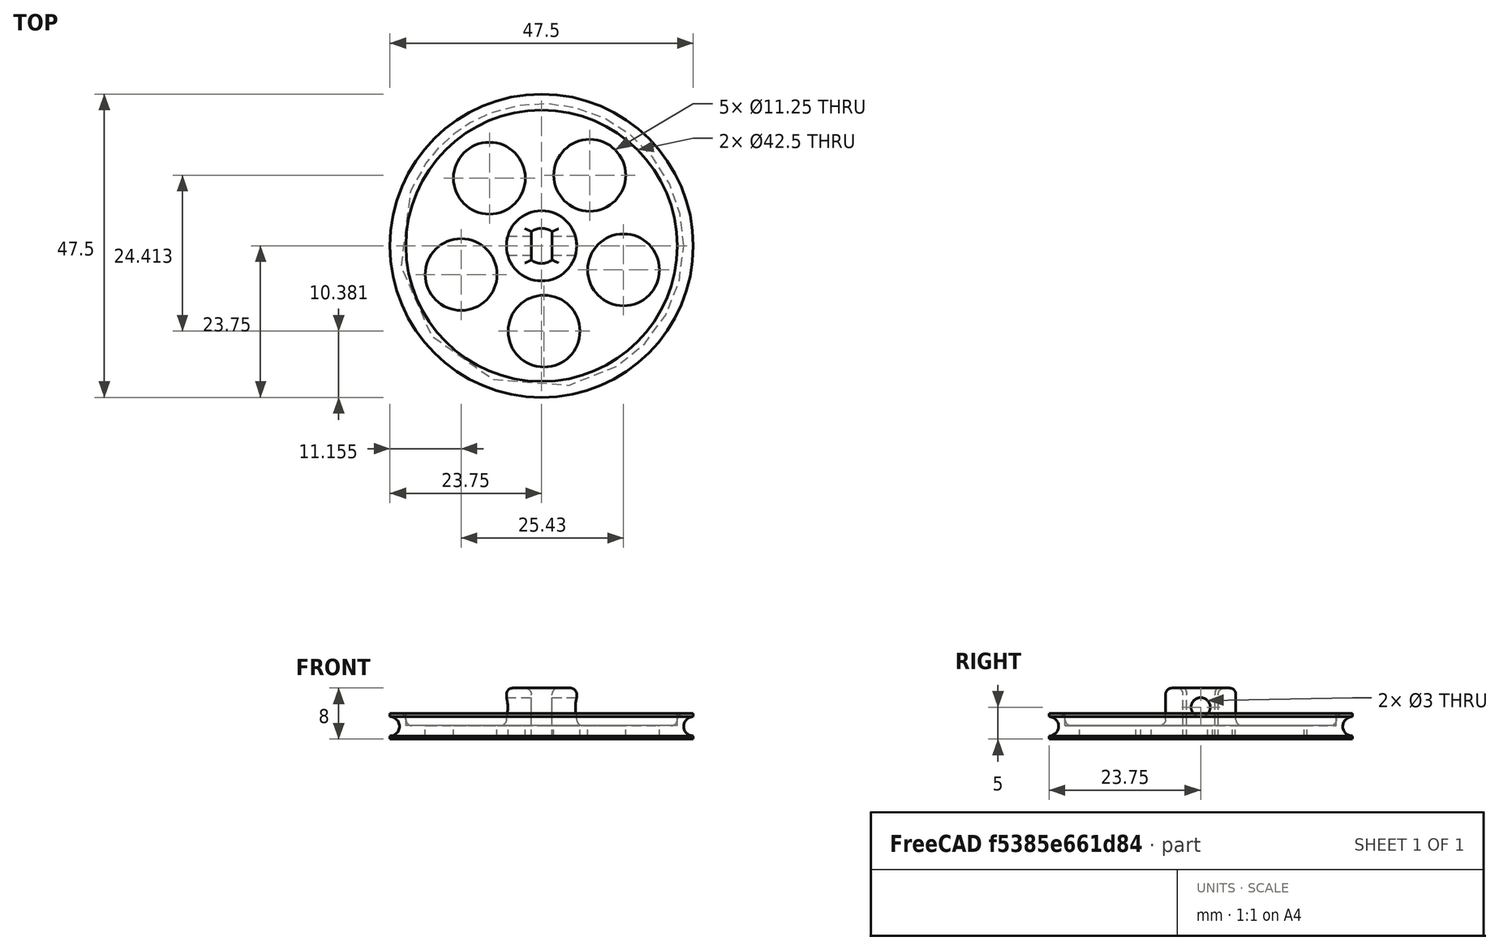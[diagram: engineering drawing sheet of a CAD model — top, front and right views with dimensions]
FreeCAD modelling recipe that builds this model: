
FCSTD DOCUMENT  (FreeCAD 0.16R6712 (Git))
Label: wheel_v02
License: All rights reserved
LicenseURL: http://en.wikipedia.org/wiki/All_rights_reserved
objects: Part::Cylinder×6, Part::Cut×5, Sketcher::SketchObject×1, Part::Torus×1, Part::Box×1, Part::MultiCommon×1, Part::FeaturePython×1, Drawing::FeaturePage×1, Part::MultiFuse×1, Spreadsheet::Sheet×1, PartDesign::Fillet×1
note: 18 computed .brp shape members not serialized (recipe doc carries the construction recipe); baked Part::Feature solids carry a one-line shape summary decoded from their .brp

FEATURE [Sketcher::SketchObject] Sketch
FEATURE [Part::Torus] Torus
  Angle1 = -180
  Angle2 = 180
  Angle3 = 360
  Placement = pos=(0,0,2) rot=(0,0,1;0rad)
  Radius1 = 23.75
  Radius2 = 1.5
  expr: Radius1 = data.wheel_diameter / 2
FEATURE [Part::Cylinder] Cylinder
  Angle = 360
  Height = 4
  Radius = 23.75
  expr: Height = data.rim_thickness
  expr: Radius = data.wheel_diameter / 2
FEATURE [Part::Cut] Cut  label="rim"
  Base = -> Cylinder
  Tool = -> Torus
FEATURE [Part::Cylinder] Cylinder001  label="hub"
  Angle = 360
  Height = 8
  Radius = 5.5
FEATURE [Part::Cylinder] Cylinder002  label="Cylinder001"
  Angle = 360
  Height = 12
  Radius = 2.75
FEATURE [Part::Box] Box  label="Cube"
  Height = 12
  Length = 3.25
  Placement = pos=(-1.6125,-6,0) rot=(0,0,1;0rad)
  Width = 12
FEATURE [Part::MultiCommon] Common  label="shaft"
  Shapes = -> [Box,Cylinder002]
FEATURE [Part::Cylinder] Cylinder003  label="setscrew"
  Angle = 360
  Height = 20
  Placement = pos=(-10,0,5) rot=(0,1,0;1.5708rad)
  Radius = 1.5
FEATURE [Part::Cylinder] Cylinder004  label="spoke"
  Angle = 360
  Height = 20
  Placement = pos=(13.375,0,0) rot=(0,0,1;0rad)
  Radius = 5.625
  expr: Radius = (data.wheel_diameter / 2 - 5.5mm) / 2 - 3.5mm
  expr: Placement.Base.x = (data.wheel_diameter / 2 - 2.5mm) / 2 + 2.75mm
FEATURE [Part::FeaturePython] Array  # Draft array (typed FeaturePython)
  Angle = 360
  ArrayType = 1
  Axis = (0,0,1)
  Base = -> Cylinder004
  Center = (0,0,0)
  Fuse = false
  IntervalAxis = (0,0,0)
  IntervalX = (1,0,0)
  IntervalY = (0,1,0)
  IntervalZ = (0,0,0)
  NumberPolar = 5
  NumberX = 1
  NumberY = 2
  NumberZ = 1
  Placement = pos=(0,0,0) rot=(0,0,1;2.22812rad)
  expr: NumberPolar = data.spokes
FEATURE [Drawing::FeaturePage] Page
  EditableTexts = AUTHOR NAME | CREATION DATE | SUPERVISOR NAME | CHECK DATE | SCALE | WEIGHT | NUMBER | SHEET | TITLE | SUBTITLE
FEATURE [Part::Cylinder] Cylinder005  label="Cylinder002"
  Angle = 360
  Height = 10
  Placement = pos=(0,0,2.1) rot=(0,0,1;0rad)
  Radius = 21.25
  expr: Radius = data.wheel_diameter / 2 - 2.5mm
FEATURE [Part::Cut] Cut002
  Base = -> Cut
  Tool = -> Cylinder005
FEATURE [Part::MultiFuse] Fusion
  Shapes = -> [Cylinder001,Cut002]
FEATURE [Part::Cut] Cut003
  Base = -> Fusion
  Tool = -> Common
FEATURE [Part::Cut] Cut004
  Base = -> Cut003
  Tool = -> Cylinder003
FEATURE [Part::Cut] Cut005
  Base = -> Cut004
  Tool = -> Array
FEATURE [Spreadsheet::Sheet] Spreadsheet  label="data"
  cells = A3=wheel_diameter; B3(wheel_diameter)==47.5mm; A4=rim_thickness; B4(rim_thickness)==4mm; A5=spokes; B5(spokes)=5
FEATURE [PartDesign::Fillet] Fillet
  Base = -> Cut005 [Edge4,Edge3,Edge2,Edge5,Edge1,Edge6,Edge27,Edge36]
  Radius = 1
